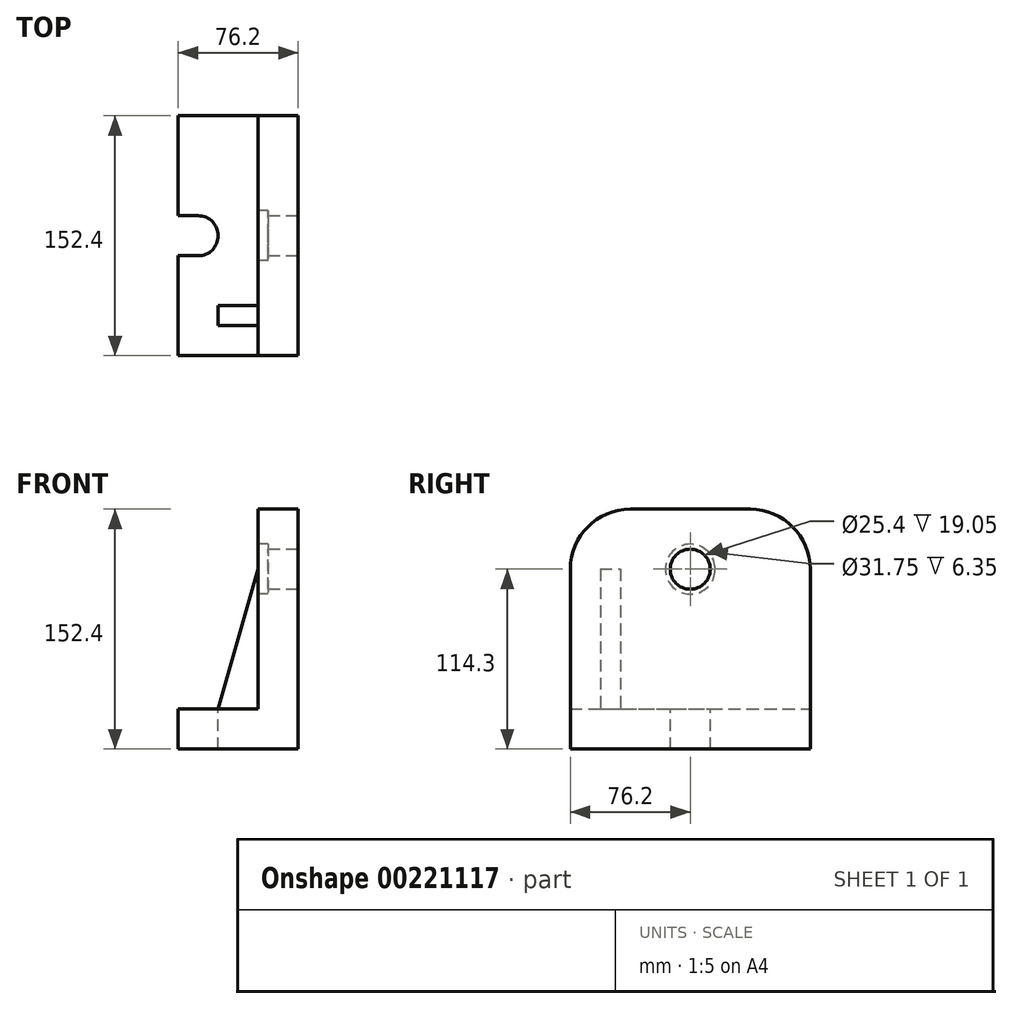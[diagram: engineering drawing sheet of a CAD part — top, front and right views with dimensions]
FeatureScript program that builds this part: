
annotation { "Feature Type Name" : "Feature", "Feature Type Description" : "" }
export const myFeature = defineFeature(function(context is Context, id is Id, definition is map)
    precondition{}
    {
        {
            var Q0;
            Q0=qCreatedBy(makeId("Front.planeOp"),FACE);
            var sketch = newSketch(context, id + "F0", { "sketchPlane" : qUnion([Q0])});
            skLineSegment(sketch, "E0", {"start": v(0, 0) * mm, "end": v(0, 152.4) * mm});
            skLineSegment(sketch, "E1", {"start": v(0, 152.4) * mm, "end": v(-25.4, 152.4) * mm});
            skLineSegment(sketch, "E2", {"start": v(-25.4, 152.4) * mm, "end": v(-25.4, 25.4) * mm});
            skLineSegment(sketch, "E3", {"start": v(-25.4, 25.4) * mm, "end": v(-76.2, 25.4) * mm});
            skLineSegment(sketch, "E4", {"start": v(-76.2, 25.4) * mm, "end": v(-76.2, 0) * mm});
            skLineSegment(sketch, "E5", {"start": v(-76.2, 0) * mm, "end": v(0, 0) * mm});
            skSolve(sketch);
        }
        {
            var Q0;
            Q0=makeQuery(id+"F0.imprint","IMPRINT",FACE,{"disambiguationData":[TD([[makeQuery(id+"F0.imprint","IMPRINT",EDGE,{"derivedFrom":sQuery(id+"F0.wireOp",EDGE,"E0")}),1.0]])]});
            extrude(context, id + "F1", {"entities" : qUnion([Q0]), "endBound" : BoundingType.SYMMETRIC, "depth" : 152.4 * mm});
        }
        {
            var Q0;
            Q0=makeQuery(id+"F1.opExtrude","SWEPT_FACE",FACE,{"disambiguationData":[OSD([sQuery(id+"F0.wireOp",EDGE,"E0")])]});
            var sketch = newSketch(context, id + "F2", { "sketchPlane" : qUnion([Q0])});
            skCircle(sketch, "E6", {"center": v(0, 114.3) * mm, "radius": 12.7 * mm});
            skSolve(sketch);
        }
        {
            var Q0;
            Q0=makeQuery(id+"F2.imprint","IMPRINT",FACE,{"disambiguationData":[TD([[makeQuery(id+"F2.imprint","IMPRINT",EDGE,{"derivedFrom":sQuery(id+"F2.wireOp",EDGE,"E6")}),1.0]])]});
            var Q1;
            Q1=sQuery(id+"F2.wireOp",EDGE,"E6");
            extrude(context, id + "F3", {"entities" : qUnion([Q0]), "operationType" : NewBodyOperationType.REMOVE, "surfaceEntities" : qUnion([Q1]), "endBound" : BoundingType.THROUGH_ALL, "oppositeDirection" : true, "depth" : 25.4 * mm});
        }
        {
            var Q0;
            Q0=makeQuery(id+"F1.opExtrude","SWEPT_FACE",FACE,{"disambiguationData":[OSD([sQuery(id+"F0.wireOp",EDGE,"E3")])]});
            var sketch = newSketch(context, id + "F4", { "sketchPlane" : qUnion([Q0])});
            skLineSegment(sketch, "E7", {"start": v(-76.2, 0) * mm, "end": v(-76.2, 12.7) * mm});
            skLineSegment(sketch, "E8", {"start": v(-76.2, 0) * mm, "end": v(-76.2, -12.7) * mm});
            skLineSegment(sketch, "E9", {"start": v(-76.2, 12.7) * mm, "end": v(-63.5, 12.7) * mm});
            skLineSegment(sketch, "E10", {"start": v(-76.2, -12.7) * mm, "end": v(-63.5, -12.7) * mm});
            skArc(sketch, "E11", {"start": v(-63.5, -12.7) * mm, "mid": v(-50.8, 0) * mm, "end": v(-63.5, 12.7) * mm});
            skSolve(sketch);
        }
        {
            var Q0;
            Q0=makeQuery(id+"F4.imprint","IMPRINT",FACE,{"disambiguationData":[TD([[makeQuery(id+"F4.imprint","IMPRINT",EDGE,{"derivedFrom":sQuery(id+"F4.wireOp",EDGE,"E7")}),-1.0]])]});
            extrude(context, id + "F5", {"entities" : qUnion([Q0]), "operationType" : NewBodyOperationType.REMOVE, "endBound" : BoundingType.THROUGH_ALL, "oppositeDirection" : true, "depth" : 25.4 * mm});
        }
        {
            var Q0;
            Q0=makeQuery(id+"F1.opExtrude","CAP_EDGE",EDGE,{"disambiguationData":[OSD([sQuery(id+"F0.wireOp",EDGE,"E1")])],"isStart":false});
            fillet(context, id + "F6", {"entities" : qUnion([Q0]), "radius" : 38.1 * mm, "tangentPropagation" : true, "allowEdgeOverflow" : false});
        }
        {
            var Q0;
            Q0=makeQuery(id+"F1.opExtrude","CAP_EDGE",EDGE,{"disambiguationData":[OSD([sQuery(id+"F0.wireOp",EDGE,"E1")])],"isStart":true});
            fillet(context, id + "F7", {"entities" : qUnion([Q0]), "radius" : 38.1 * mm, "tangentPropagation" : true, "allowEdgeOverflow" : false});
        }
        {
            var Q0;
            Q0=makeQuery(id+"F1.opExtrude","SWEPT_FACE",FACE,{"disambiguationData":[OSD([sQuery(id+"F0.wireOp",EDGE,"E2")])]});
            var sketch = newSketch(context, id + "F8", { "sketchPlane" : qUnion([Q0])});
            skCircle(sketch, "E12", {"center": v(0, 114.3) * mm, "radius": 15.88 * mm});
            skSolve(sketch);
        }
        {
            var Q0;
            Q0=makeQuery(id+"F8.imprint","IMPRINT",FACE,{"disambiguationData":[TD([[makeQuery(id+"F8.imprint","IMPRINT",EDGE,{"derivedFrom":sQuery(id+"F8.wireOp",EDGE,"E12")}),1.0]])]});
            extrude(context, id + "F9", {"entities" : qUnion([Q0]), "operationType" : NewBodyOperationType.REMOVE, "oppositeDirection" : true, "depth" : 6.35 * mm});
        }
        {
            var Q0;
            Q0=qCreatedBy(makeId("Front.planeOp"),FACE);
            cPlane(context, id + "F10", {"entities" : qUnion([Q0]), "cplaneType" : CPlaneType.OFFSET, "offset" : 44.45 * mm, "width" : 152.4 * mm, "height" : 152.4 * mm});
        }
        {
            var Q0;
            Q0=qCreatedBy(id+"F10.planeOp",FACE);
            var sketch = newSketch(context, id + "F11", { "sketchPlane" : qUnion([Q0])});
            skLineSegment(sketch, "E13.0", {"start": v(-25.4, 25.4) * mm, "end": v(-50.8, 25.4) * mm});
            skLineSegment(sketch, "E13.1", {"start": v(-25.4, 114.3) * mm, "end": v(-25.4, 25.4) * mm});
            skPoint(sketch, "E14.orphan", {"position": v(-76.2, 25.4) * mm});
            skLineSegment(sketch, "E15", {"start": v(-50.8, 25.4) * mm, "end": v(-25.4, 114.3) * mm});
            skSolve(sketch);
        }
        {
            var Q0;
            Q0=makeQuery(id+"F11.imprint","IMPRINT",FACE,{"disambiguationData":[TD([[makeQuery(id+"F11.imprint","IMPRINT",EDGE,{"derivedFrom":sQuery(id+"F11.wireOp",EDGE,"E13.0")}),-1.0]])]});
            extrude(context, id + "F12", {"entities" : qUnion([Q0]), "operationType" : NewBodyOperationType.ADD, "depth" : 12.7 * mm});
        }
    });
